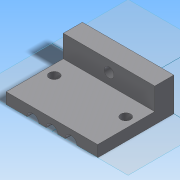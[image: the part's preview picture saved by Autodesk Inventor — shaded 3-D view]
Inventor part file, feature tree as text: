
AUTODESK INVENTOR PART (.ipt)
format: ipt  version: 2014 SP2 (Build 180246200, 246)  size: 135,680 bytes
history: native  units: in
note: dims shown in document units (in); Inventor stores cm internally (conversion verified against a paired STEP export)
features: sketch x4, extrude x4, hole x2, mirror x1, projected_geometry x1
ambient origin geometry x8: Origin, YZ Plane, XZ Plane, XY Plane, X Axis, Y Axis, Z Axis, Center Point
bodies: Solid1 (feature_tree)
feature tree (12):
  sketch  "Sketch1"  dims[d0=0.1775in d3=0.25in]
  extrude  "Extrusion1"  Depth=0.25in
  extrude  "Extrusion2"  Depth=0.15in
  extrude  "Extrusion3"  Depth=1.0in TaperAngle=0.0deg
  hole  "Hole1"  [1 undecoded]
  mirror  "Mirror1"
  sketch  "Sketch7"  dims[d9=0.81in d10=0.0in d11=0.16in d12=0.19in d13=0.0in d15=0.129in d16=0.75in d17=0.225in d18=0.188in d19=0.5635in d20=1.0in d21=0.8108in d27=0.25in d28=0.0in d29=0.129in d30=0.75in d31=0.225in d32=0.188in d33=0.5635in d34=1.0in d35=0.8108in d36=0.145in]
  extrude  "Extrusion5"  Depth=0.19in TaperAngle=0.0deg
  hole  "Hole2"  [1 undecoded]
  sketch  "Sketch2"  dims[d4=0.25in d5=0.15in]
  sketch  "Sketch3"  dims[d6=1.2in d7=1.0in d8=0.0in]
  projected_geometry  "Projected Loop1"
note: 2 required parameter values undecoded (feature->parameter linkage not recoverable at this tier; creation-order binding heuristic only, values carry confidence <= 0.55)
